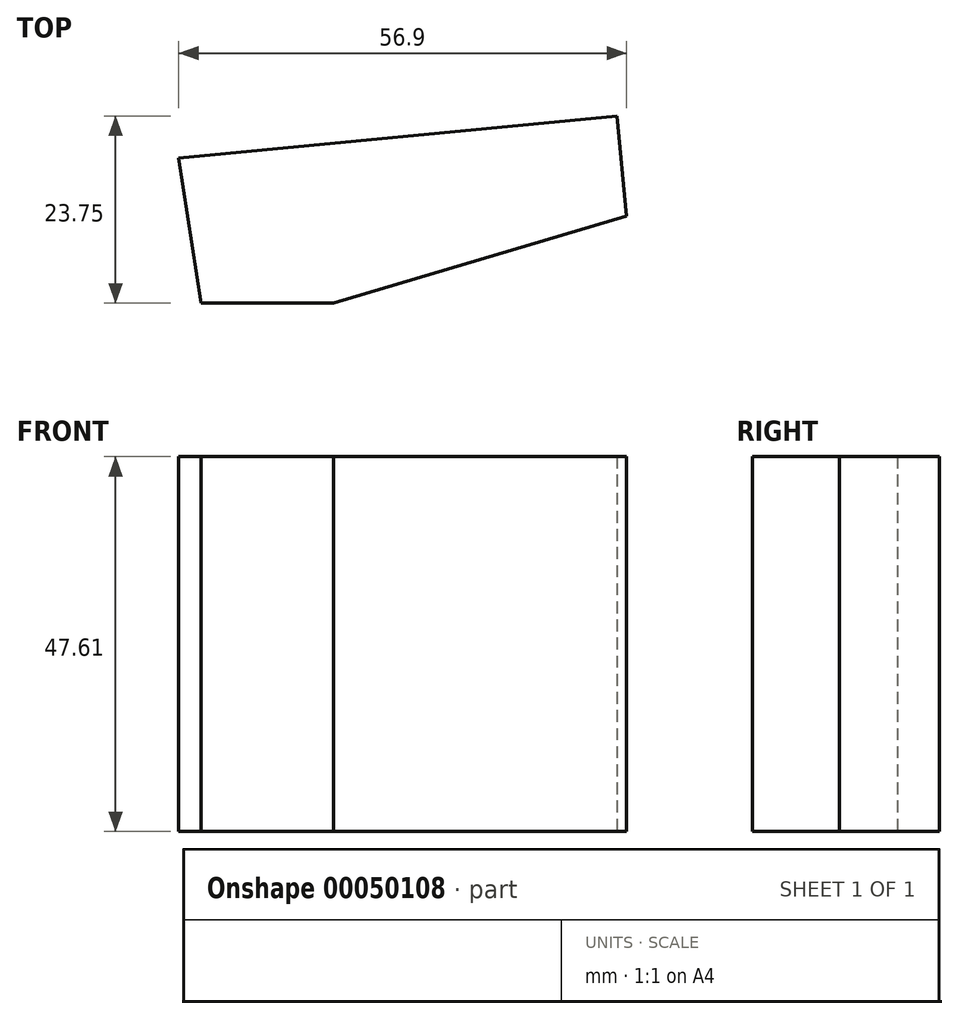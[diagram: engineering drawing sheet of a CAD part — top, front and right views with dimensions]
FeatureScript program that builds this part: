
annotation { "Feature Type Name" : "Feature", "Feature Type Description" : "" }
export const myFeature = defineFeature(function(context is Context, id is Id, definition is map)
    precondition{}
    {
        {
            var Q0;
            Q0=qCreatedBy(makeId("Top.planeOp"),FACE);
            var sketch = newSketch(context, id + "F0", { "sketchPlane" : qUnion([Q0])});
            skLineSegment(sketch, "E0.bottom", {"start": v(-56.18, 43.41) * mm, "end": v(11.88, 43.41) * mm});
            skLineSegment(sketch, "E0.top", {"start": v(-56.18, -22.3) * mm, "end": v(11.88, -22.3) * mm});
            skLineSegment(sketch, "E0.left", {"start": v(-56.18, 43.41) * mm, "end": v(-56.18, -22.3) * mm});
            skLineSegment(sketch, "E0.right", {"start": v(11.88, 43.41) * mm, "end": v(11.88, -22.3) * mm});
            skCircle(sketch, "E1", {"center": v(-29.28, 15.1) * mm, "radius": 19.1 * mm});
            skLineSegment(sketch, "E2", {"start": v(-17, -45.91) * mm, "end": v(38.7, -40.59) * mm});
            skLineSegment(sketch, "E3", {"start": v(38.7, -40.59) * mm, "end": v(39.9, -53.28) * mm});
            skLineSegment(sketch, "E4", {"start": v(39.9, -53.28) * mm, "end": v(2.66, -64.34) * mm});
            skLineSegment(sketch, "E5", {"start": v(2.66, -64.34) * mm, "end": v(-14.13, -64.34) * mm});
            skLineSegment(sketch, "E6", {"start": v(-14.13, -64.34) * mm, "end": v(-17, -45.91) * mm});
            skSolve(sketch);
        }
        {
            var Q0;
            Q0=makeQuery(id+"F0.imprint","IMPRINT",FACE,{"disambiguationData":[TD([[makeQuery(id+"F0.imprint","IMPRINT",EDGE,{"derivedFrom":sQuery(id+"F0.wireOp",EDGE,"E2")}),-1.0]])]});
            extrude(context, id + "F1", {"entities" : qUnion([Q0]), "depth" : 47.6 * mm});
        }
    });
